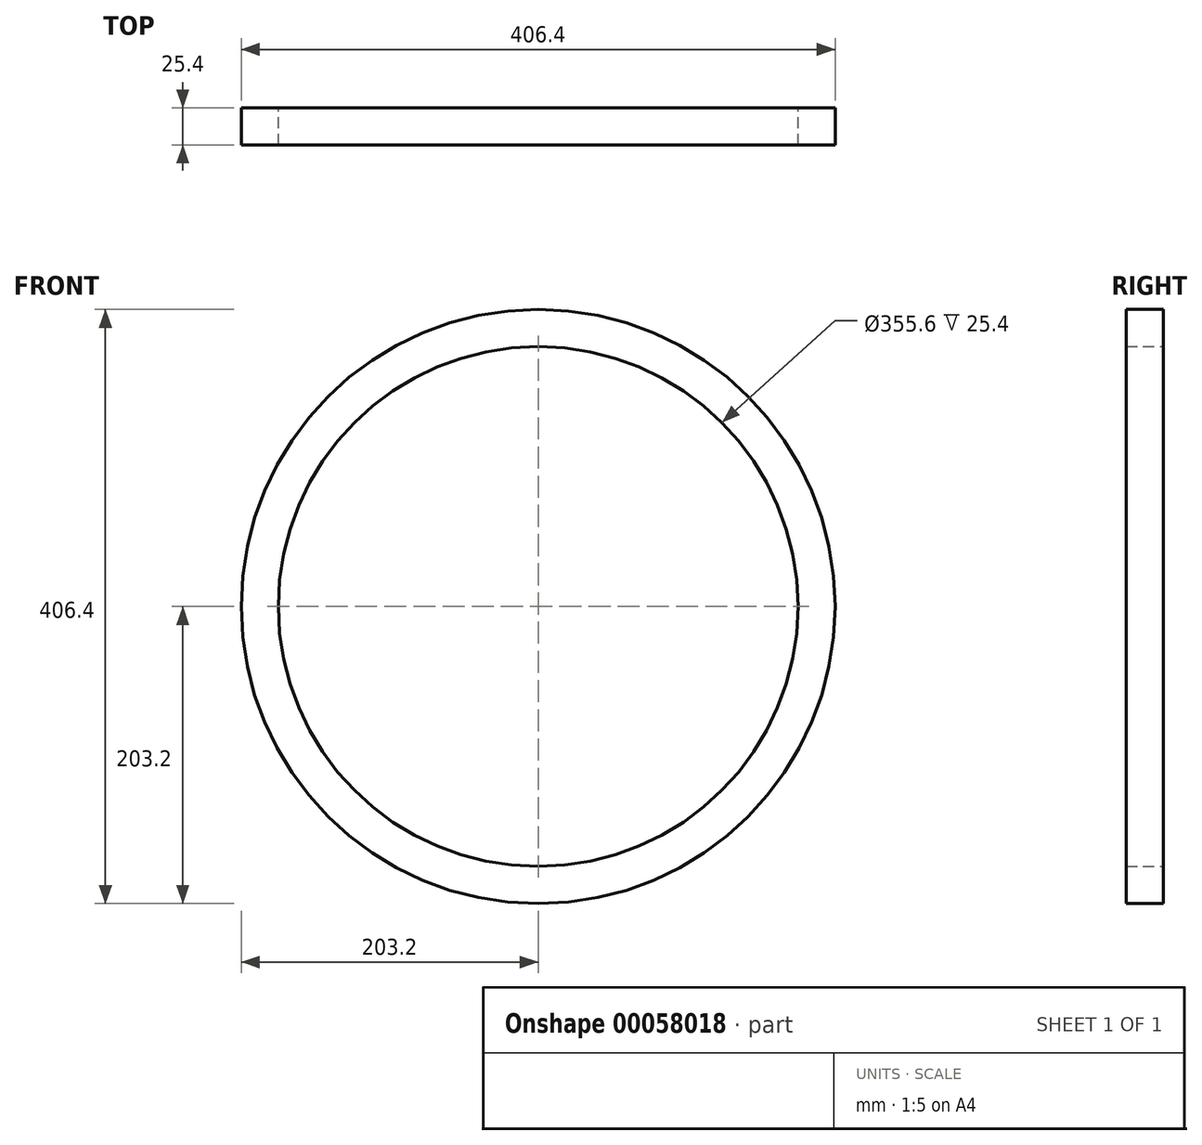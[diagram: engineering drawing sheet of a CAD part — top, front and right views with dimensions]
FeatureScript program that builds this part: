
annotation { "Feature Type Name" : "Feature", "Feature Type Description" : "" }
export const myFeature = defineFeature(function(context is Context, id is Id, definition is map)
    precondition{}
    {
        {
            var Q0;
            Q0=qCreatedBy(makeId("Front.planeOp"),FACE);
            var sketch = newSketch(context, id + "F0", { "sketchPlane" : qUnion([Q0])});
            skCircle(sketch, "E0", {"center": v(0, 0) * mm, "radius": 203.2 * mm});
            skCircle(sketch, "E1", {"center": v(0, 0) * mm, "radius": 177.8 * mm});
            skSolve(sketch);
        }
        {
            var Q0;
            Q0=makeQuery(id+"F0.imprint","IMPRINT",FACE,{"disambiguationData":[TD([[makeQuery(id+"F0.imprint","IMPRINT",EDGE,{"derivedFrom":sQuery(id+"F0.wireOp",EDGE,"E0")}),1.0]])]});
            extrude(context, id + "F1", {"entities" : qUnion([Q0]), "depth" : 25.4 * mm});
        }
    });
